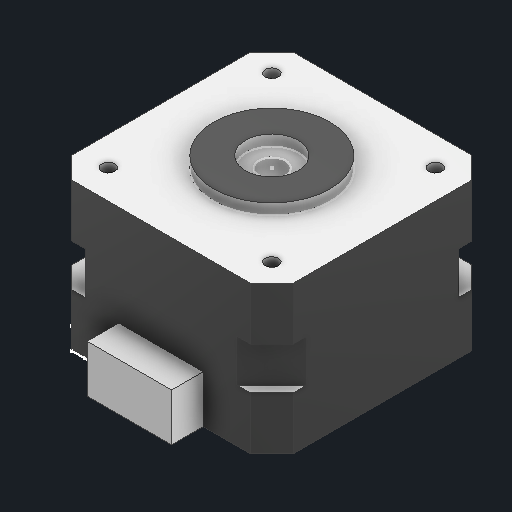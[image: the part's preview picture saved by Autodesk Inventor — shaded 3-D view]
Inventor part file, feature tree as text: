
AUTODESK INVENTOR PART (.ipt)
format: ipt  version: 2023 (Build 270158000, 158)  size: 160,256 bytes
history: native  units: mm
features: sketch x2, other x1
ambient origin geometry x8: Origin, YZ Plane, XZ Plane, XY Plane, X Axis, Y Axis, Z Axis, Center Point
bodies: Solid2 (feature_tree), Solid1 (feature_tree)
feature tree (3):
  other  "Repaired Geometry1"
  sketch  "Sketch2"
  sketch  "Sketch1"
